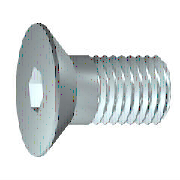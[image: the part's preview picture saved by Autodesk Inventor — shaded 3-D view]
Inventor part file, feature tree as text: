
AUTODESK INVENTOR PART (.ipt)
format: ipt  version: 2012 (Build 160160000, 160)  size: 179,712 bytes
history: native  units: mm (DEFAULTED — no unit token found)
features: extrude x1, plane x1
ambient origin geometry x7: Origin, YZ Plane, XY Plane, X Axis, Y Axis, Z Axis, Center Point
bodies: Solid1 (feature_tree), Body (feature_tree)
feature tree (2):
  extrude  "Slot"  Depth=19.05mm
  plane  "Work Plane1"
